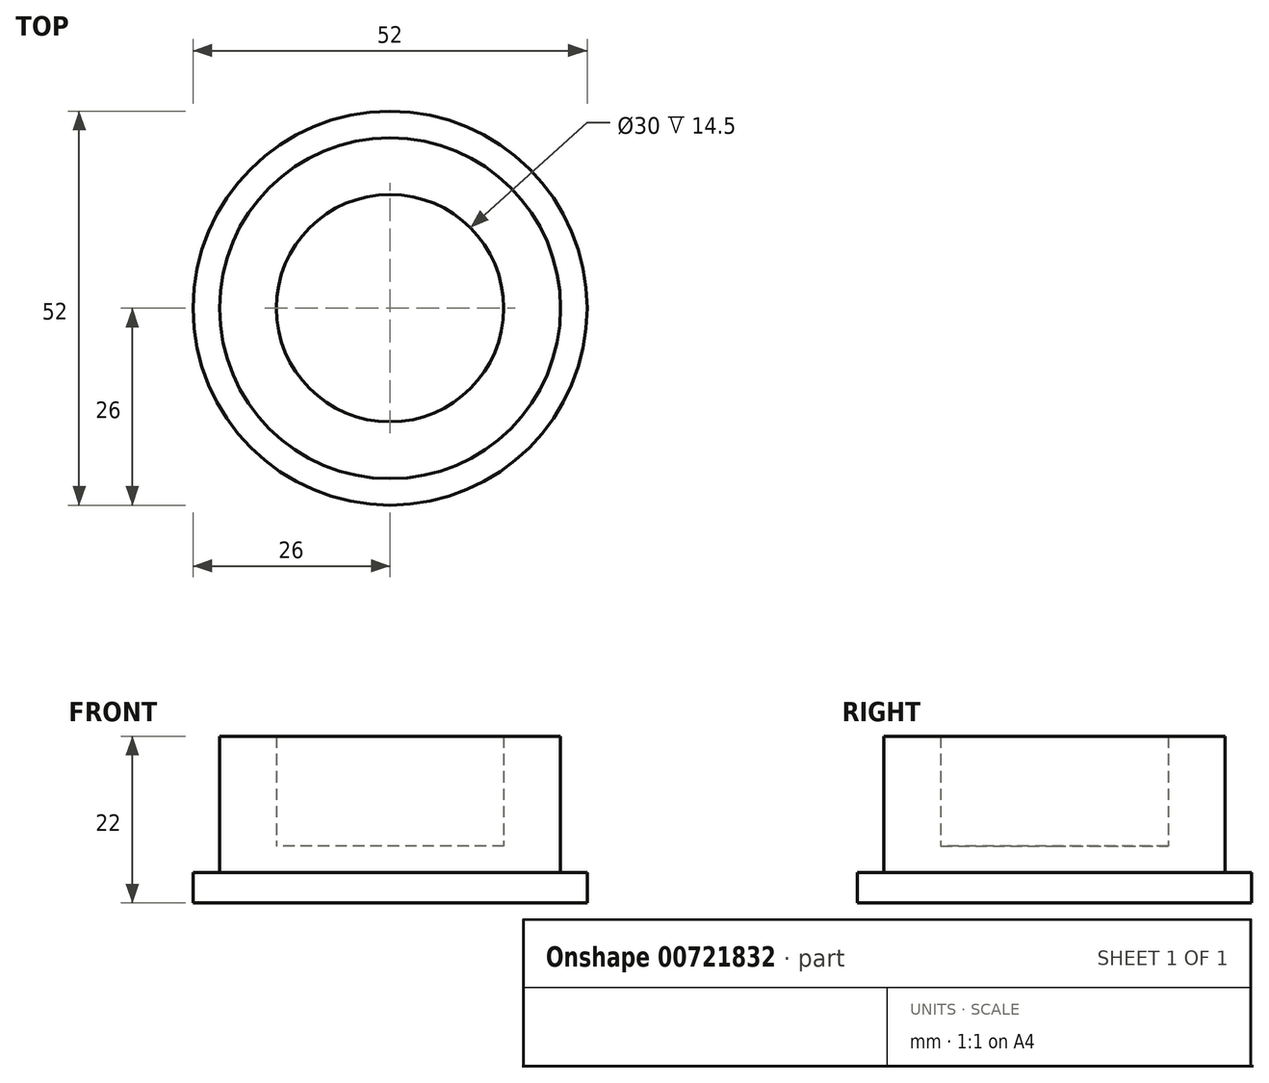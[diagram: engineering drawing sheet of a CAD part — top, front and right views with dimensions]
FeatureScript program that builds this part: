
annotation { "Feature Type Name" : "Feature", "Feature Type Description" : "" }
export const myFeature = defineFeature(function(context is Context, id is Id, definition is map)
    precondition{}
    {
        {
            var Q0;
            Q0=qCreatedBy(makeId("Top.planeOp"),FACE);
            var sketch = newSketch(context, id + "F0", { "sketchPlane" : qUnion([Q0])});
            skCircle(sketch, "E0", {"center": v(0, 0) * mm, "radius": 26 * mm});
            skCircle(sketch, "E1", {"center": v(0, 0) * mm, "radius": 22.5 * mm});
            skSolve(sketch);
        }
        {
            var Q0;
            Q0=makeQuery(id+"F0.imprint","IMPRINT",FACE,{"disambiguationData":[TD([[makeQuery(id+"F0.imprint","IMPRINT",EDGE,{"derivedFrom":sQuery(id+"F0.wireOp",EDGE,"E0")}),1.0]])]});
            extrude(context, id + "F1", {"entities" : qUnion([Q0]), "depth" : 4 * mm, "offsetDistance" : 25 * mm});
        }
        {
            var Q0;
            Q0=makeQuery(id+"F0.imprint","IMPRINT",FACE,{"disambiguationData":[TD([[makeQuery(id+"F0.imprint","IMPRINT",EDGE,{"derivedFrom":sQuery(id+"F0.wireOp",EDGE,"E1")}),1.0]])]});
            extrude(context, id + "F2", {"entities" : qUnion([Q0]), "operationType" : NewBodyOperationType.ADD, "depth" : 22 * mm, "offsetDistance" : 25 * mm});
        }
        {
            var Q0;
            Q0=makeQuery(id+"F2.opExtrude","CAP_FACE",FACE,{"disambiguationData":[OSD([sQuery(id+"F0.wireOp",EDGE,"E1")])],"isStart":false});
            shell(context, id + "F3", {"entities" : qUnion([Q0]), "thickness" : 7.5 * mm});
        }
    });
